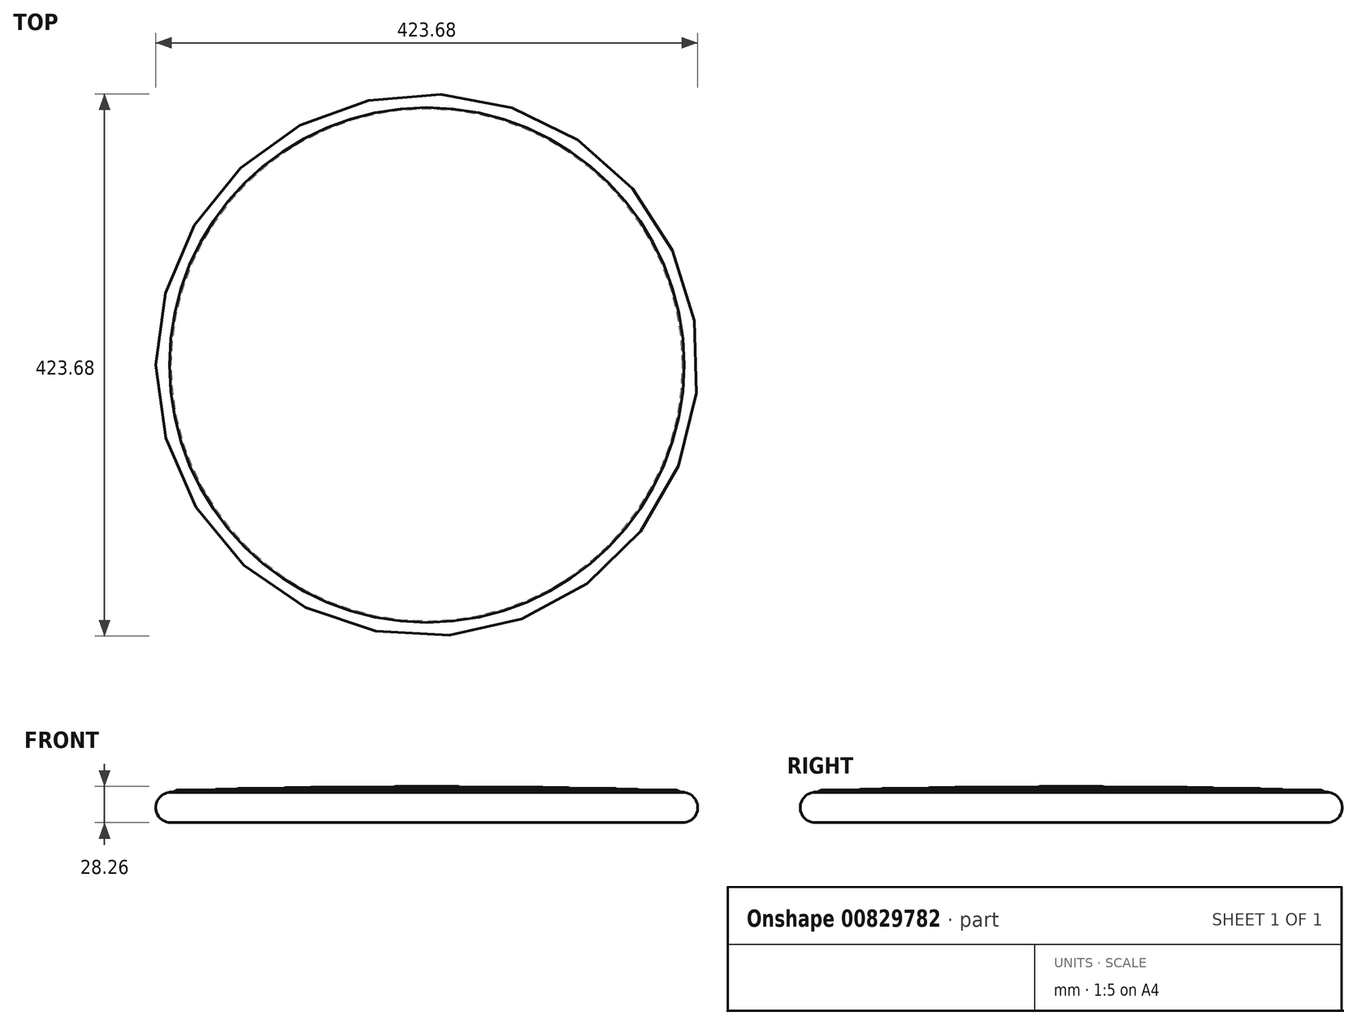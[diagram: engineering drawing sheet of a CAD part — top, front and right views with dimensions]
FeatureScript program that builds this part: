
annotation { "Feature Type Name" : "Feature", "Feature Type Description" : "" }
export const myFeature = defineFeature(function(context is Context, id is Id, definition is map)
    precondition{}
    {
        {
            var Q0;
            Q0=qCreatedBy(makeId("Front.planeOp"),FACE);
            var sketch = newSketch(context, id + "F0", { "sketchPlane" : qUnion([Q0])});
            skLineSegment(sketch, "E0", {"start": v(0, 0) * mm, "end": v(-200, 0) * mm});
            skLineSegment(sketch, "E1", {"start": v(0, 0) * mm, "end": v(0, 23.39) * mm});
            skArc(sketch, "E2", {"start": v(-200, 23.68) * mm, "mid": v(-211.84, 11.84) * mm, "end": v(-200, 0) * mm});
            skArc(sketch, "E3", {"start": v(-20.05, 26.18) * mm, "mid": v(-24.16, 28.25) * mm, "end": v(-28.13, 25.91) * mm});
            skArc(sketch, "E4", {"start": v(-43.78, 25.72) * mm, "mid": v(-47, 27.42) * mm, "end": v(-50.21, 25.73) * mm});
            skArc(sketch, "E5", {"start": v(-65.33, 25.47) * mm, "mid": v(-69.12, 27.72) * mm, "end": v(-72.78, 25.24) * mm});
            skArc(sketch, "E6", {"start": v(-86.56, 25.65) * mm, "mid": v(-90.17, 27.64) * mm, "end": v(-93.6, 25.35) * mm});
            skArc(sketch, "E7", {"start": v(-107.03, 25.77) * mm, "mid": v(-110.17, 27.3) * mm, "end": v(-113.16, 25.47) * mm});
            skArc(sketch, "E8", {"start": v(-126.66, 25.55) * mm, "mid": v(-129, 26.68) * mm, "end": v(-131.34, 25.55) * mm});
            skArc(sketch, "E9", {"start": v(-144.66, 25.55) * mm, "mid": v(-147, 26.68) * mm, "end": v(-149.34, 25.55) * mm});
            skArc(sketch, "E10", {"start": v(-161.84, 25.2) * mm, "mid": v(-163.98, 26.12) * mm, "end": v(-166.12, 25.24) * mm});
            skArc(sketch, "E11", {"start": v(-178, 24.9) * mm, "mid": v(-180.03, 25.65) * mm, "end": v(-182.04, 24.85) * mm});
            skArc(sketch, "E12", {"start": v(-193.3, 24.85) * mm, "mid": v(-195.04, 25.38) * mm, "end": v(-196.76, 24.8) * mm});
            skLineSegment(sketch, "E13.trimOffspring", {"start": v(-200, 23.68) * mm, "end": v(-201.17, 23.98) * mm});
            skLineSegment(sketch, "E14.trimOffspring", {"start": v(-186.79, 23.22) * mm, "end": v(-189.3, 23.43) * mm});
            skLineSegment(sketch, "E15.trimOffspring", {"start": v(-169.88, 23.68) * mm, "end": v(-174.82, 23.68) * mm});
            skLineSegment(sketch, "E16.trimOffspring", {"start": v(-153.24, 23.68) * mm, "end": v(-158.25, 23.68) * mm});
            skLineSegment(sketch, "E17.trimOffspring", {"start": v(-135.24, 23.68) * mm, "end": v(-140.76, 23.68) * mm});
            skLineSegment(sketch, "E18.trimOffspring", {"start": v(-116.24, 23.68) * mm, "end": v(-122.76, 23.68) * mm});
            skLineSegment(sketch, "E19.trimOffspring", {"start": v(-96.26, 23.65) * mm, "end": v(-102.94, 23.65) * mm});
            skLineSegment(sketch, "E20.trimOffspring", {"start": v(-75.25, 23.63) * mm, "end": v(-83.14, 23.65) * mm});
            skLineSegment(sketch, "E21.trimOffspring", {"start": v(-54.35, 23.56) * mm, "end": v(-62.27, 23.58) * mm});
            skLineSegment(sketch, "E22.trimOffspring", {"start": v(-32.44, 23.48) * mm, "end": v(-39.62, 23.5) * mm});
            skLineSegment(sketch, "E23.trimOffspring", {"start": v(0, 23.39) * mm, "end": v(-14.8, 23.43) * mm});
            skPoint(sketch, "E24.visualSharp", {"position": v(-19.2, 23.44) * mm});
            skArc(sketch, "E24.filletArc", {"start": v(-20.05, 26.18) * mm, "mid": v(-17.76, 24.16) * mm, "end": v(-14.8, 23.43) * mm});
            skPoint(sketch, "E25.visualSharp", {"position": v(-28.8, 23.47) * mm});
            skArc(sketch, "E25.filletArc", {"start": v(-32.44, 23.48) * mm, "mid": v(-29.96, 24.12) * mm, "end": v(-28.13, 25.91) * mm});
            skPoint(sketch, "E26.visualSharp", {"position": v(-43.1, 23.51) * mm});
            skArc(sketch, "E26.filletArc", {"start": v(-43.78, 25.72) * mm, "mid": v(-41.97, 24.1) * mm, "end": v(-39.62, 23.5) * mm});
            skPoint(sketch, "E27.visualSharp", {"position": v(-50.9, 23.54) * mm});
            skArc(sketch, "E27.filletArc", {"start": v(-54.35, 23.56) * mm, "mid": v(-52.01, 24.13) * mm, "end": v(-50.21, 25.73) * mm});
            skPoint(sketch, "E28.visualSharp", {"position": v(-64.88, 23.6) * mm});
            skArc(sketch, "E28.filletArc", {"start": v(-65.33, 25.47) * mm, "mid": v(-64.07, 24.1) * mm, "end": v(-62.27, 23.58) * mm});
            skPoint(sketch, "E29.visualSharp", {"position": v(-73.12, 23.62) * mm});
            skArc(sketch, "E29.filletArc", {"start": v(-75.25, 23.63) * mm, "mid": v(-73.77, 24.06) * mm, "end": v(-72.78, 25.24) * mm});
            skPoint(sketch, "E30.visualSharp", {"position": v(-86.04, 23.66) * mm});
            skArc(sketch, "E30.filletArc", {"start": v(-86.56, 25.65) * mm, "mid": v(-85.12, 24.2) * mm, "end": v(-83.14, 23.65) * mm});
            skPoint(sketch, "E31.visualSharp", {"position": v(-93.96, 23.65) * mm});
            skArc(sketch, "E31.filletArc", {"start": v(-96.26, 23.65) * mm, "mid": v(-94.68, 24.1) * mm, "end": v(-93.6, 25.35) * mm});
            skPoint(sketch, "E32.visualSharp", {"position": v(-106.37, 23.65) * mm});
            skArc(sketch, "E32.filletArc", {"start": v(-107.03, 25.77) * mm, "mid": v(-105.25, 24.2) * mm, "end": v(-102.94, 23.65) * mm});
            skPoint(sketch, "E33.visualSharp", {"position": v(-113.63, 23.68) * mm});
            skArc(sketch, "E33.filletArc", {"start": v(-116.24, 23.68) * mm, "mid": v(-114.46, 24.16) * mm, "end": v(-113.16, 25.47) * mm});
            skPoint(sketch, "E34.visualSharp", {"position": v(-126, 23.68) * mm});
            skArc(sketch, "E34.filletArc", {"start": v(-126.66, 25.55) * mm, "mid": v(-124.92, 24.17) * mm, "end": v(-122.76, 23.68) * mm});
            skPoint(sketch, "E35.visualSharp", {"position": v(-132, 23.68) * mm});
            skArc(sketch, "E35.filletArc", {"start": v(-135.24, 23.68) * mm, "mid": v(-133.08, 24.17) * mm, "end": v(-131.34, 25.55) * mm});
            skPoint(sketch, "E36.visualSharp", {"position": v(-144, 23.68) * mm});
            skArc(sketch, "E36.filletArc", {"start": v(-144.66, 25.55) * mm, "mid": v(-142.92, 24.17) * mm, "end": v(-140.76, 23.68) * mm});
            skPoint(sketch, "E37.visualSharp", {"position": v(-150, 23.68) * mm});
            skArc(sketch, "E37.filletArc", {"start": v(-153.24, 23.68) * mm, "mid": v(-151.08, 24.17) * mm, "end": v(-149.34, 25.55) * mm});
            skPoint(sketch, "E38.visualSharp", {"position": v(-161.05, 23.68) * mm});
            skArc(sketch, "E38.filletArc", {"start": v(-161.84, 25.2) * mm, "mid": v(-160.2, 24.08) * mm, "end": v(-158.25, 23.68) * mm});
            skPoint(sketch, "E39.visualSharp", {"position": v(-166.95, 23.68) * mm});
            skArc(sketch, "E39.filletArc", {"start": v(-169.88, 23.68) * mm, "mid": v(-167.85, 24.08) * mm, "end": v(-166.12, 25.24) * mm});
            skPoint(sketch, "E40.visualSharp", {"position": v(-177.18, 23.68) * mm});
            skArc(sketch, "E40.filletArc", {"start": v(-178, 24.9) * mm, "mid": v(-176.52, 24) * mm, "end": v(-174.82, 23.68) * mm});
            skPoint(sketch, "E41.visualSharp", {"position": v(-182.99, 22.9) * mm});
            skArc(sketch, "E41.filletArc", {"start": v(-186.79, 23.22) * mm, "mid": v(-184.24, 23.54) * mm, "end": v(-182.04, 24.85) * mm});
            skPoint(sketch, "E42.visualSharp", {"position": v(-192.3, 23.68) * mm});
            skArc(sketch, "E42.filletArc", {"start": v(-193.3, 24.85) * mm, "mid": v(-191.4, 23.88) * mm, "end": v(-189.3, 23.43) * mm});
            skPoint(sketch, "E43.visualSharp", {"position": v(-197.9, 23.13) * mm});
            skArc(sketch, "E43.filletArc", {"start": v(-201.17, 23.98) * mm, "mid": v(-198.87, 23.9) * mm, "end": v(-196.76, 24.8) * mm});
            skSolve(sketch);
        }
        {
            var Q0;
            Q0=makeQuery(id+"F0.imprint","IMPRINT",FACE,{"disambiguationData":[TD([[makeQuery(id+"F0.imprint","IMPRINT",EDGE,{"derivedFrom":sQuery(id+"F0.wireOp",EDGE,"E0")}),-1.0]])]});
            var Q1;
            Q1=sQuery(id+"F0.wireOp",EDGE,"E1");
            revolve(context, id + "F1", {"surfaceOperationType" : NewSurfaceOperationType.NEW, "entities" : qUnion([Q0]), "axis" : qUnion([Q1]), "revolveType" : RevolveType.FULL});
        }
    });
